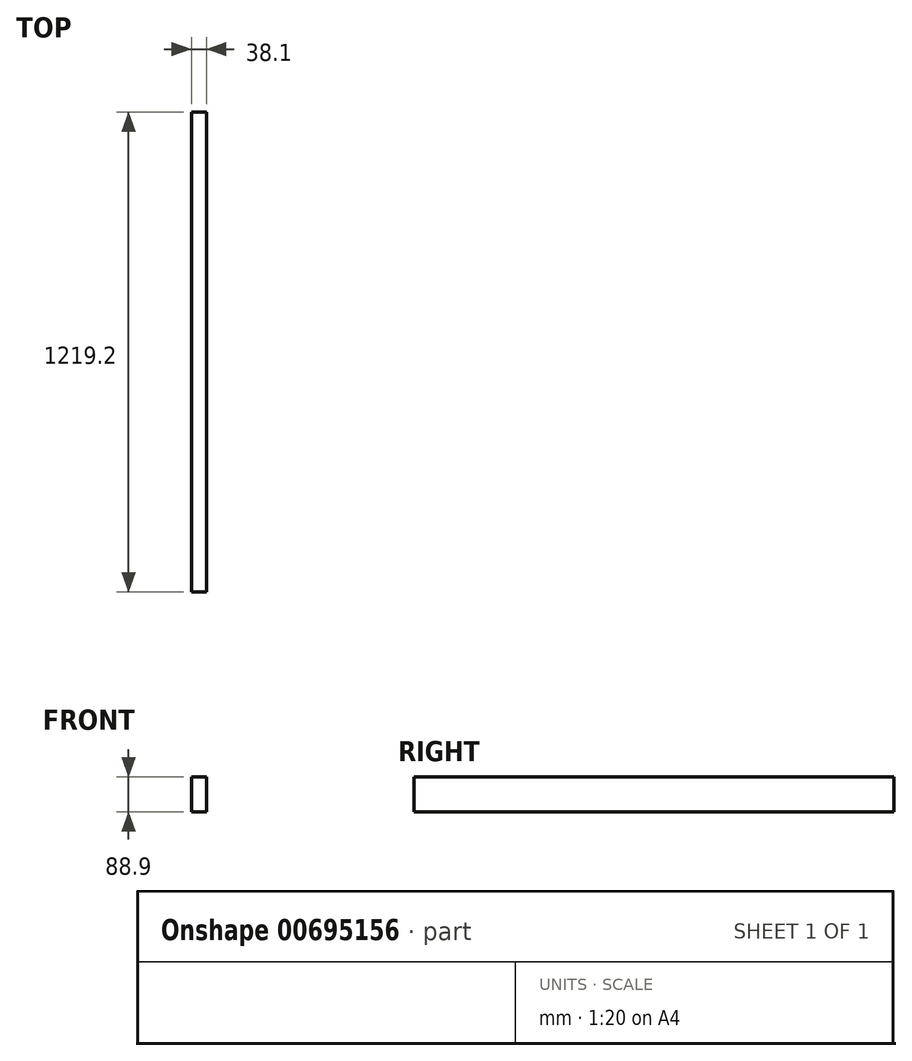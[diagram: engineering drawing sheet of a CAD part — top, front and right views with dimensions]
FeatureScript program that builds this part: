
annotation { "Feature Type Name" : "Feature", "Feature Type Description" : "" }
export const myFeature = defineFeature(function(context is Context, id is Id, definition is map)
    precondition{}
    {
        {
            var Q0;
            Q0=qCreatedBy(makeId("Front.planeOp"),FACE);
            var sketch = newSketch(context, id + "F0", { "sketchPlane" : qUnion([Q0])});
            skLineSegment(sketch, "E0.bottom", {"start": v(192.53, 202.94) * mm, "end": v(230.63, 202.94) * mm});
            skLineSegment(sketch, "E0.top", {"start": v(192.53, 114.04) * mm, "end": v(230.63, 114.04) * mm});
            skLineSegment(sketch, "E0.left", {"start": v(192.53, 202.94) * mm, "end": v(192.53, 114.04) * mm});
            skLineSegment(sketch, "E0.right", {"start": v(230.63, 202.94) * mm, "end": v(230.63, 114.04) * mm});
            skSolve(sketch);
        }
        {
            var Q0;
            Q0=makeQuery(id+"F0.imprint","IMPRINT",FACE,{"disambiguationData":[TD([[makeQuery(id+"F0.imprint","IMPRINT",EDGE,{"derivedFrom":sQuery(id+"F0.wireOp",EDGE,"E0.bottom")}),-1.0]])]});
            extrude(context, id + "F1", {"entities" : qUnion([Q0]), "depth" : 1219.2 * mm, "offsetDistance" : 25.4 * mm});
        }
    });
